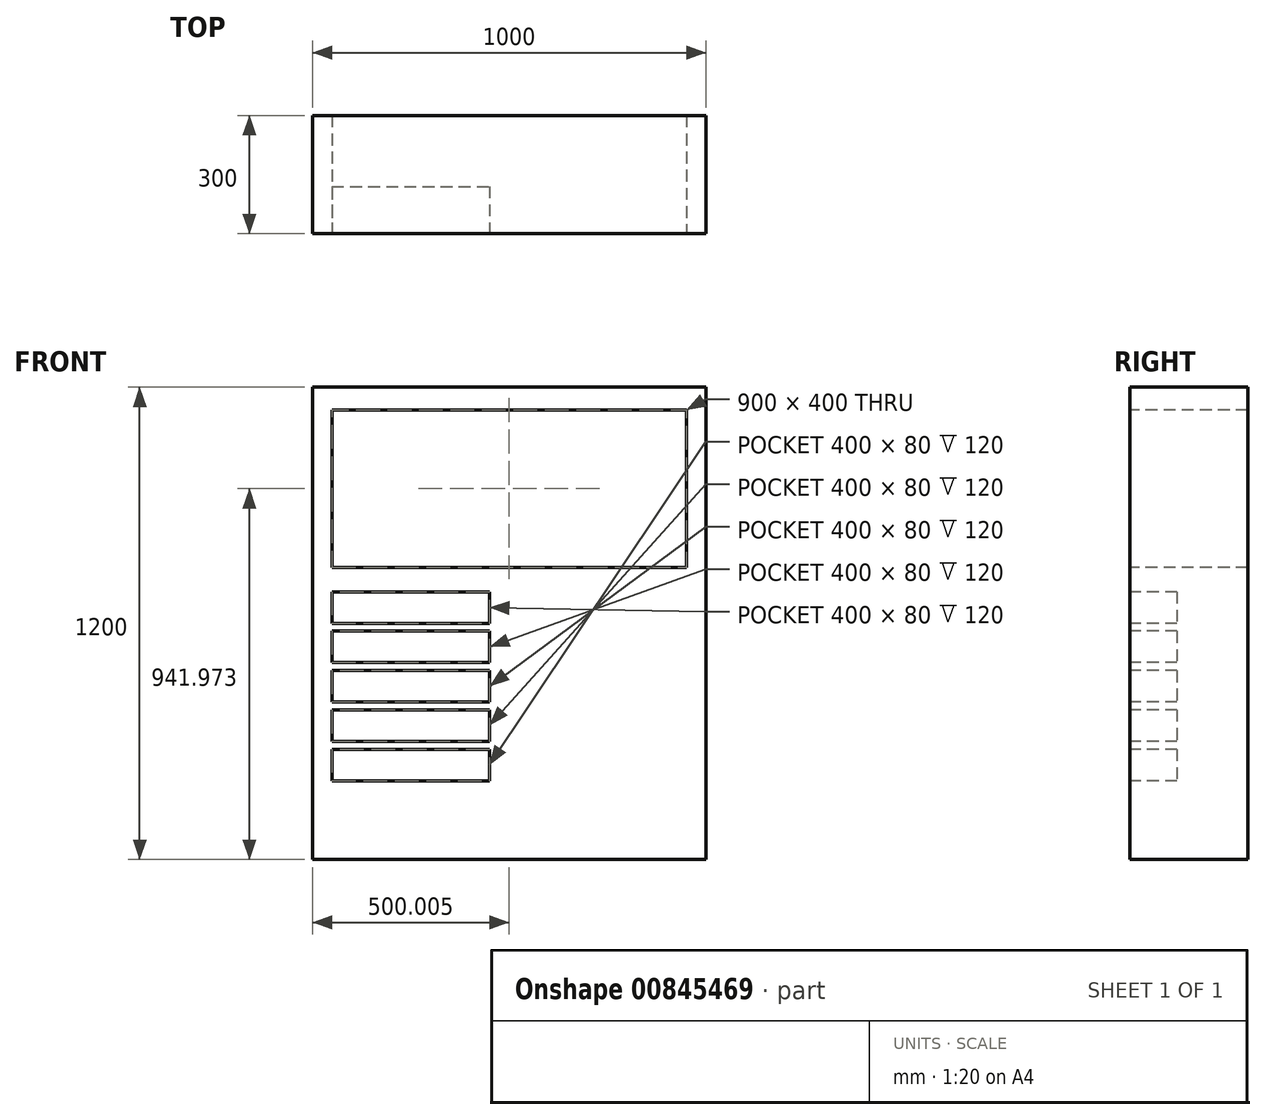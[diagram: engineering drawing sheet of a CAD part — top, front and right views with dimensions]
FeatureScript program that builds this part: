
annotation { "Feature Type Name" : "Feature", "Feature Type Description" : "" }
export const myFeature = defineFeature(function(context is Context, id is Id, definition is map)
    precondition{}
    {
        {
            var Q0;
            Q0=qCreatedBy(makeId("Top.planeOp"),FACE);
            var sketch = newSketch(context, id + "F0", { "sketchPlane" : qUnion([Q0])});
            skLineSegment(sketch, "E0.bottom", {"start": v(497.02, 150) * mm, "end": v(-502.98, 150) * mm});
            skLineSegment(sketch, "E0.top", {"start": v(497.02, -150) * mm, "end": v(-502.98, -150) * mm});
            skLineSegment(sketch, "E0.left", {"start": v(497.02, 150) * mm, "end": v(497.02, -150) * mm});
            skLineSegment(sketch, "E0.right", {"start": v(-502.98, 150) * mm, "end": v(-502.98, -150) * mm});
            skPoint(sketch, "E0.middle", {"position": v(-2.98, 0) * mm});
            skSolve(sketch);
        }
        {
            var Q0;
            Q0=makeQuery(id+"F0.imprint","IMPRINT",FACE,{"disambiguationData":[TD([[makeQuery(id+"F0.imprint","IMPRINT",EDGE,{"derivedFrom":sQuery(id+"F0.wireOp",EDGE,"E0.bottom")}),1.0]])]});
            extrude(context, id + "F1", {"entities" : qUnion([Q0]), "depth" : 1200 * mm, "offsetDistance" : 25 * mm});
        }
        {
            var Q0;
            Q0=makeQuery(id+"F1.opExtrude","SWEPT_FACE",FACE,{"disambiguationData":[OSD([sQuery(id+"F0.wireOp",EDGE,"E0.top")])]});
            var sketch = newSketch(context, id + "F2", { "sketchPlane" : qUnion([Q0])});
            skLineSegment(sketch, "E1.bottom", {"start": v(-452.98, 680) * mm, "end": v(-52.98, 680) * mm});
            skLineSegment(sketch, "E1.top", {"start": v(-452.98, 600) * mm, "end": v(-52.98, 600) * mm});
            skLineSegment(sketch, "E1.left", {"start": v(-452.98, 680) * mm, "end": v(-452.98, 600) * mm});
            skLineSegment(sketch, "E1.right", {"start": v(-52.98, 680) * mm, "end": v(-52.98, 600) * mm});
            skLineSegment(sketch, "E2.0.1.0", {"start": v(-452.98, 500) * mm, "end": v(-52.98, 500) * mm});
            skLineSegment(sketch, "E2.0.1.1", {"start": v(-452.98, 580) * mm, "end": v(-52.98, 580) * mm});
            skLineSegment(sketch, "E2.0.1.2", {"start": v(-52.98, 580) * mm, "end": v(-52.98, 500) * mm});
            skLineSegment(sketch, "E2.0.1.3", {"start": v(-452.98, 580) * mm, "end": v(-452.98, 500) * mm});
            skLineSegment(sketch, "E2.0.2.0", {"start": v(-452.98, 400) * mm, "end": v(-52.98, 400) * mm});
            skLineSegment(sketch, "E2.0.2.1", {"start": v(-452.98, 480) * mm, "end": v(-52.98, 480) * mm});
            skLineSegment(sketch, "E2.0.2.2", {"start": v(-52.98, 480) * mm, "end": v(-52.98, 400) * mm});
            skLineSegment(sketch, "E2.0.2.3", {"start": v(-452.98, 480) * mm, "end": v(-452.98, 400) * mm});
            skLineSegment(sketch, "E2.0.3.0", {"start": v(-452.98, 300) * mm, "end": v(-52.98, 300) * mm});
            skLineSegment(sketch, "E2.0.3.1", {"start": v(-452.98, 380) * mm, "end": v(-52.98, 380) * mm});
            skLineSegment(sketch, "E2.0.3.2", {"start": v(-52.98, 380) * mm, "end": v(-52.98, 300) * mm});
            skLineSegment(sketch, "E2.0.3.3", {"start": v(-452.98, 380) * mm, "end": v(-452.98, 300) * mm});
            skLineSegment(sketch, "E2.0.4.0", {"start": v(-452.98, 200) * mm, "end": v(-52.98, 200) * mm});
            skLineSegment(sketch, "E2.0.4.1", {"start": v(-452.98, 280) * mm, "end": v(-52.98, 280) * mm});
            skLineSegment(sketch, "E2.0.4.2", {"start": v(-52.98, 280) * mm, "end": v(-52.98, 200) * mm});
            skLineSegment(sketch, "E2.0.4.3", {"start": v(-452.98, 280) * mm, "end": v(-452.98, 200) * mm});
            skLineSegment(sketch, "E2.direction1", {"start": v(-452.98, 600) * mm, "end": v(-427.98, 600) * mm, "construction": true});
            skLineSegment(sketch, "E2.direction2", {"start": v(-452.98, 600) * mm, "end": v(-452.98, 500) * mm, "construction": true});
            skSolve(sketch);
        }
        {
            var Q0;
            Q0 = qSketchRegion(id + "F2", true);
            extrude(context, id + "F3", {"entities" : qUnion([Q0]), "operationType" : NewBodyOperationType.REMOVE, "oppositeDirection" : true, "depth" : 120 * mm, "offsetDistance" : 25 * mm});
        }
        {
            var Q0;
            Q0=makeQuery(id+"F1.opExtrude","SWEPT_FACE",FACE,{"disambiguationData":[OSD([sQuery(id+"F0.wireOp",EDGE,"E0.top")])]});
            var sketch = newSketch(context, id + "F4", { "sketchPlane" : qUnion([Q0])});
            skLineSegment(sketch, "E3.bottom", {"start": v(-452.98, 741.97) * mm, "end": v(447.02, 741.97) * mm});
            skLineSegment(sketch, "E3.top", {"start": v(-452.98, 1141.97) * mm, "end": v(447.02, 1141.97) * mm});
            skLineSegment(sketch, "E3.left", {"start": v(-452.98, 741.97) * mm, "end": v(-452.98, 1141.97) * mm});
            skLineSegment(sketch, "E3.right", {"start": v(447.02, 741.97) * mm, "end": v(447.02, 1141.97) * mm});
            skSolve(sketch);
        }
        {
            var Q0;
            Q0=makeQuery(id+"F4.imprint","IMPRINT",FACE,{"disambiguationData":[TD([[makeQuery(id+"F4.imprint","IMPRINT",EDGE,{"derivedFrom":sQuery(id+"F4.wireOp",EDGE,"E3.bottom")}),1.0]])]});
            extrude(context, id + "F5", {"entities" : qUnion([Q0]), "operationType" : NewBodyOperationType.REMOVE, "oppositeDirection" : true, "depth" : 300 * mm, "offsetDistance" : 25 * mm});
        }
    });
